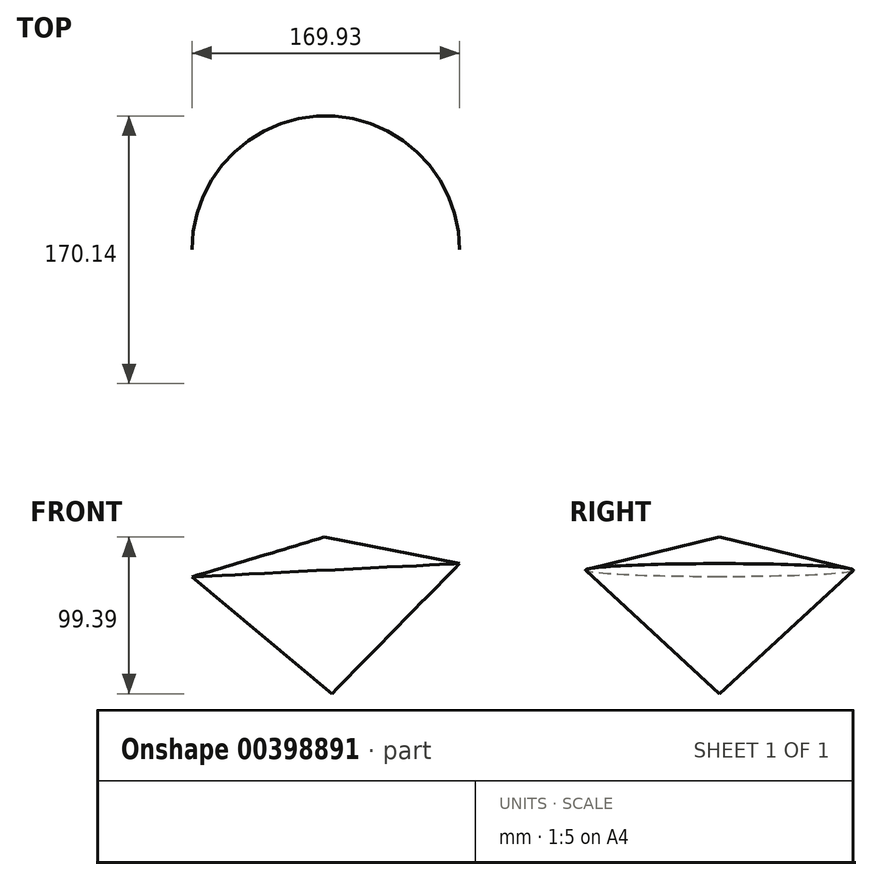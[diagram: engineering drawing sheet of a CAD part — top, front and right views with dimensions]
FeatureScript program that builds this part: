
annotation { "Feature Type Name" : "Feature", "Feature Type Description" : "" }
export const myFeature = defineFeature(function(context is Context, id is Id, definition is map)
    precondition{}
    {
        {
            var Q0;
            Q0=qCreatedBy(makeId("Front.planeOp"),FACE);
            var sketch = newSketch(context, id + "F0", { "sketchPlane" : qUnion([Q0])});
            skLineSegment(sketch, "E0", {"start": v(-57.8, 56.98) * mm, "end": v(-52.87, -42.4) * mm});
            skLineSegment(sketch, "E1", {"start": v(-57.8, 56.98) * mm, "end": v(28.2, 40.22) * mm});
            skLineSegment(sketch, "E2", {"start": v(28.2, 40.22) * mm, "end": v(-52.87, -42.4) * mm});
            skSolve(sketch);
        }
        {
            var Q0;
            Q0=makeQuery(id+"F0.imprint","IMPRINT",FACE,{"disambiguationData":[TD([[makeQuery(id+"F0.imprint","IMPRINT",EDGE,{"derivedFrom":sQuery(id+"F0.wireOp",EDGE,"E0")}),1.0]])]});
            var Q1;
            Q1=sQuery(id+"F0.wireOp",EDGE,"E0");
            revolve(context, id + "F1", {"entities" : qUnion([Q0]), "axis" : qUnion([Q1]), "revolveType" : RevolveType.FULL});
        }
    });
